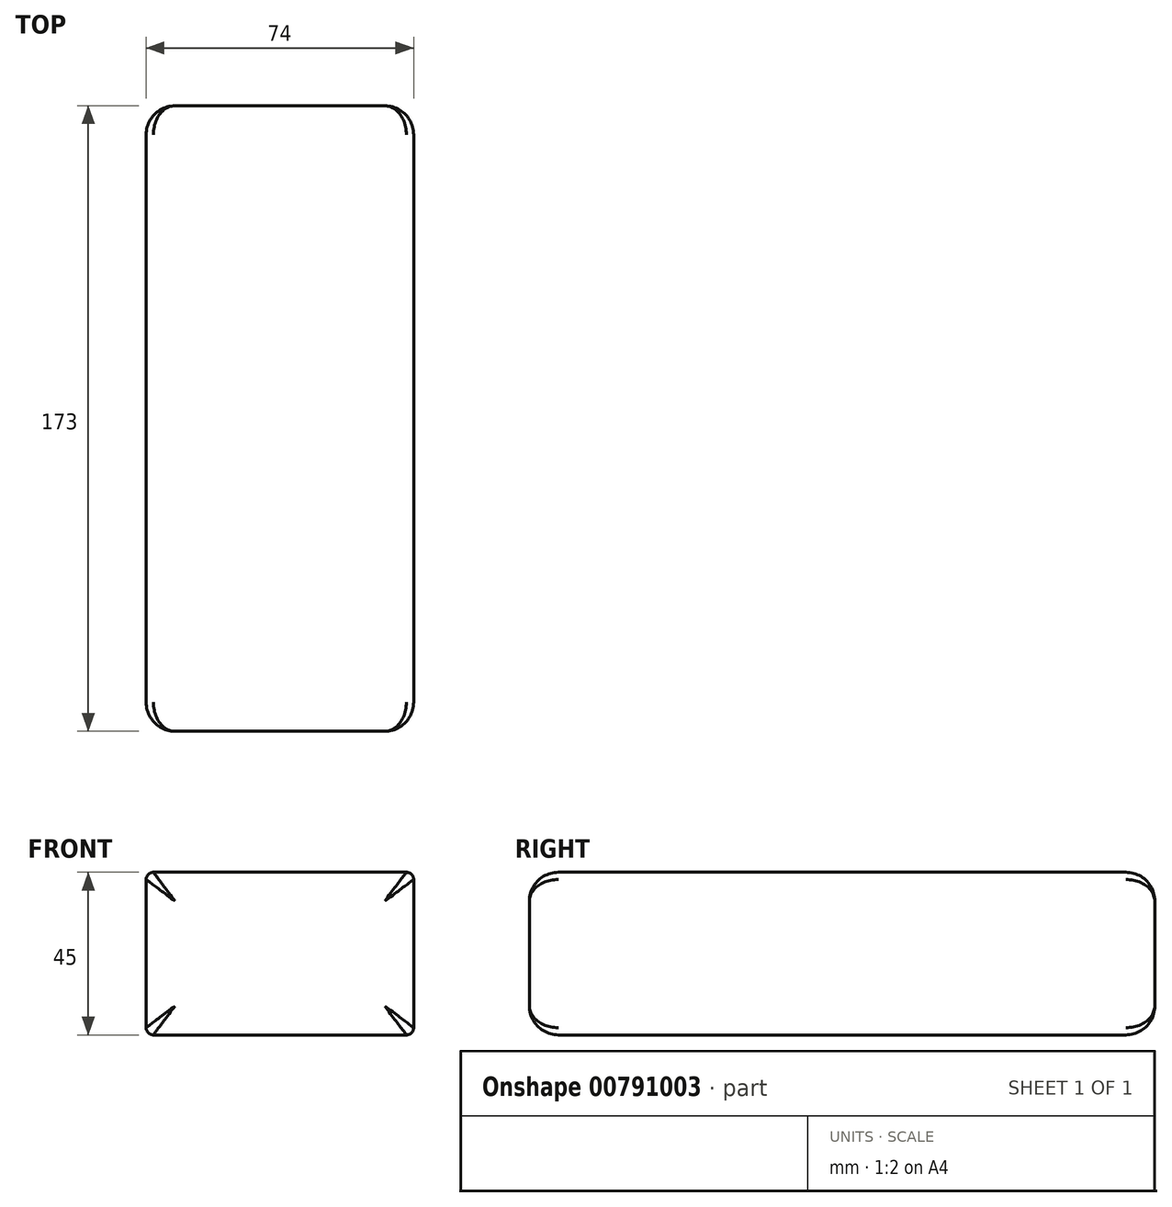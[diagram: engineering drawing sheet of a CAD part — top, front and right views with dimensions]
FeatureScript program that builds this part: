
annotation { "Feature Type Name" : "Feature", "Feature Type Description" : "" }
export const myFeature = defineFeature(function(context is Context, id is Id, definition is map)
    precondition{}
    {
        {
            var Q0;
            Q0=qCreatedBy(makeId("Right.planeOp"),FACE);
            var sketch = newSketch(context, id + "F0", { "sketchPlane" : qUnion([Q0])});
            skLineSegment(sketch, "E0.bottom", {"start": v(86.5, 22.5) * mm, "end": v(-86.5, 22.5) * mm});
            skLineSegment(sketch, "E0.top", {"start": v(86.5, -22.5) * mm, "end": v(-86.5, -22.5) * mm});
            skLineSegment(sketch, "E0.left", {"start": v(86.5, 22.5) * mm, "end": v(86.5, -22.5) * mm});
            skLineSegment(sketch, "E0.right", {"start": v(-86.5, 22.5) * mm, "end": v(-86.5, -22.5) * mm});
            skPoint(sketch, "E0.middle", {"position": v(0, 0) * mm});
            skSolve(sketch);
        }
        {
            var Q0;
            Q0=makeQuery(id+"F0.imprint","IMPRINT",FACE,{"disambiguationData":[TD([[makeQuery(id+"F0.imprint","IMPRINT",EDGE,{"derivedFrom":sQuery(id+"F0.wireOp",EDGE,"E0.bottom")}),1.0]])]});
            extrude(context, id + "F1", {"entities" : qUnion([Q0]), "endBound" : BoundingType.SYMMETRIC, "depth" : 74 * mm, "offsetDistance" : 25 * mm});
        }
        {
            var Q0;
            Q0=makeQuery(id+"F1.opExtrude","CAP_EDGE",EDGE,{"disambiguationData":[OSD([sQuery(id+"F0.wireOp",EDGE,"E0.bottom")])],"isStart":false});
            var Q1;
            Q1=makeQuery(id+"F1.opExtrude","CAP_EDGE",EDGE,{"disambiguationData":[OSD([sQuery(id+"F0.wireOp",EDGE,"E0.top")])],"isStart":false});
            var Q2;
            Q2=makeQuery(id+"F1.opExtrude","CAP_EDGE",EDGE,{"disambiguationData":[OSD([sQuery(id+"F0.wireOp",EDGE,"E0.bottom")])],"isStart":true});
            var Q3;
            Q3=makeQuery(id+"F1.opExtrude","CAP_EDGE",EDGE,{"disambiguationData":[OSD([sQuery(id+"F0.wireOp",EDGE,"E0.top")])],"isStart":true});
            fillet(context, id + "F2", {"entities" : qUnion([Q0, Q1, Q2, Q3]), "radius" : 2 * mm, "tangentPropagation" : true, "allowEdgeOverflow" : false});
        }
        {
            var Q0;
            Q0=makeQuery(id+"F1.opExtrude","SWEPT_EDGE",EDGE,{"disambiguationData":[OSD([sQuery(id+"F0.wireOp",EDGE,"E0.bottom"),sQuery(id+"F0.wireOp",EDGE,"E0.right")])]});
            var Q1;
            Q1=makeQuery(id+"F1.opExtrude","SWEPT_EDGE",EDGE,{"disambiguationData":[OSD([sQuery(id+"F0.wireOp",EDGE,"E0.top"),sQuery(id+"F0.wireOp",EDGE,"E0.right")])]});
            var Q2;
            Q2=makeQuery(id+"F1.opExtrude","SWEPT_EDGE",EDGE,{"disambiguationData":[OSD([sQuery(id+"F0.wireOp",EDGE,"E0.bottom"),sQuery(id+"F0.wireOp",EDGE,"E0.left")])]});
            var Q3;
            Q3=makeQuery(id+"F1.opExtrude","SWEPT_EDGE",EDGE,{"disambiguationData":[OSD([sQuery(id+"F0.wireOp",EDGE,"E0.top"),sQuery(id+"F0.wireOp",EDGE,"E0.left")])]});
            fillet(context, id + "F3", {"entities" : qUnion([Q0, Q1, Q2, Q3]), "radius" : 8 * mm, "tangentPropagation" : true, "allowEdgeOverflow" : false});
        }
    });
